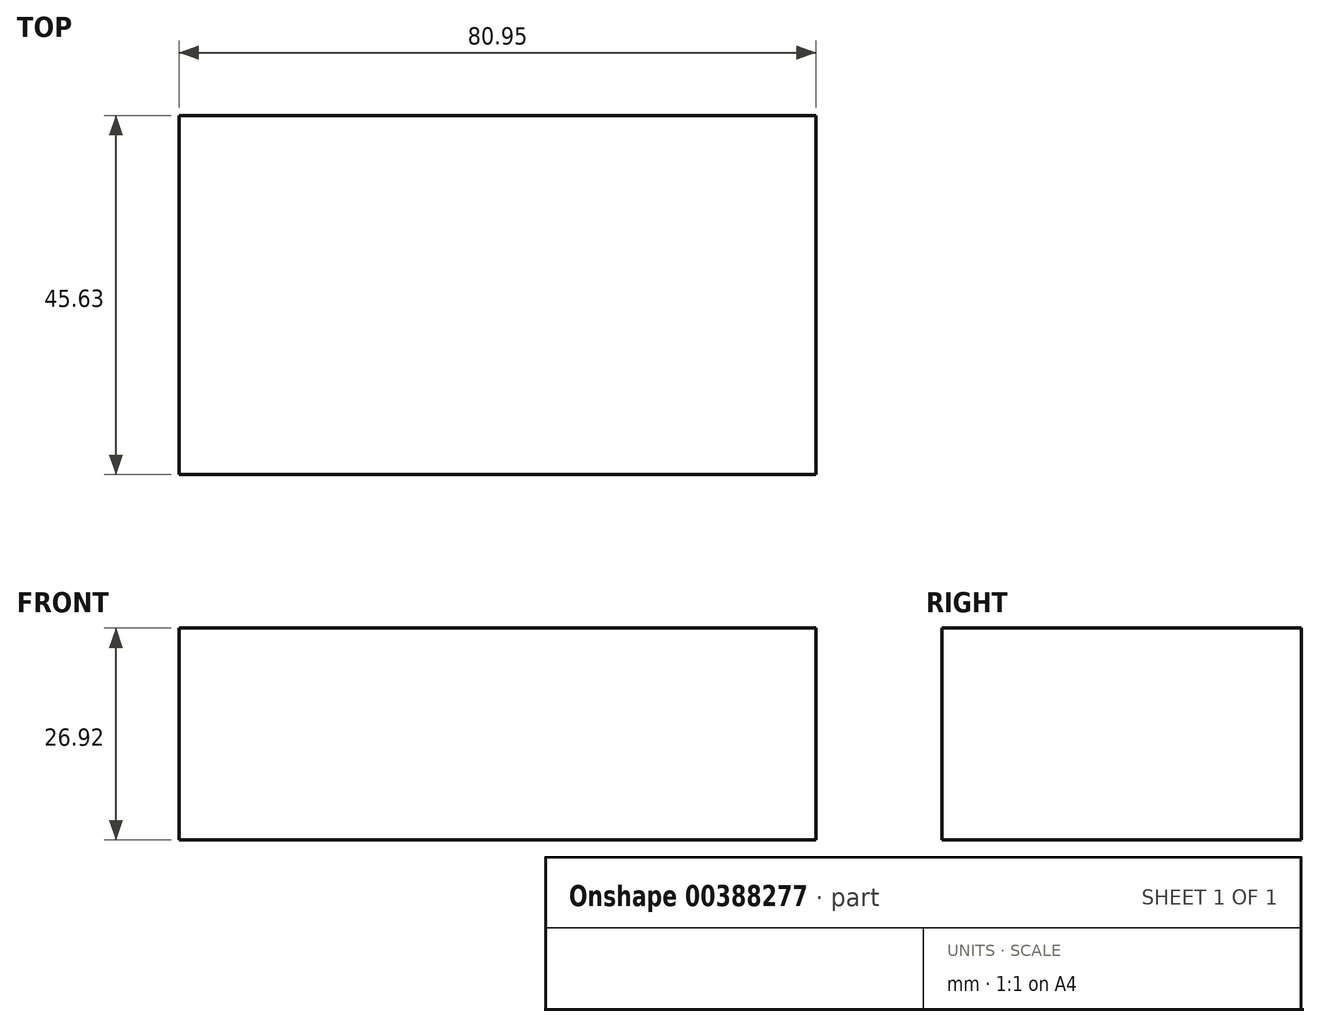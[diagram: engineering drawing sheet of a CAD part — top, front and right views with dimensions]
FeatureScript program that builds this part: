
annotation { "Feature Type Name" : "Feature", "Feature Type Description" : "" }
export const myFeature = defineFeature(function(context is Context, id is Id, definition is map)
    precondition{}
    {
        {
            var Q0;
            Q0=qCreatedBy(makeId("Top.planeOp"),FACE);
            var sketch = newSketch(context, id + "F0", { "sketchPlane" : qUnion([Q0])});
            skLineSegment(sketch, "E0.bottom", {"start": v(-36.53, 32.71) * mm, "end": v(44.42, 32.71) * mm});
            skLineSegment(sketch, "E0.top", {"start": v(-36.53, -12.92) * mm, "end": v(44.42, -12.92) * mm});
            skLineSegment(sketch, "E0.left", {"start": v(-36.53, 32.71) * mm, "end": v(-36.53, -12.92) * mm});
            skLineSegment(sketch, "E0.right", {"start": v(44.42, 32.71) * mm, "end": v(44.42, -12.92) * mm});
            skSolve(sketch);
        }
        {
            var Q0;
            Q0 = qSketchRegion(id + "F0", true);
            extrude(context, id + "F1", {"entities" : qUnion([Q0]), "depth" : 26.92 * mm});
        }
        {
            var Q0;
            Q0=qCreatedBy(makeId("Top.planeOp"),FACE);
            var sketch = newSketch(context, id + "F2", { "sketchPlane" : qUnion([Q0])});
            skLineSegment(sketch, "E1.bottom", {"start": v(-26.19, 23.43) * mm, "end": v(-20, 23.43) * mm});
            skLineSegment(sketch, "E1.top", {"start": v(-26.19, 0) * mm, "end": v(-20, 0) * mm});
            skLineSegment(sketch, "E1.left", {"start": v(-26.19, 23.43) * mm, "end": v(-26.19, 0) * mm});
            skLineSegment(sketch, "E1.right", {"start": v(-20, 23.43) * mm, "end": v(-20, 0) * mm});
            skArc(sketch, "E2", {"start": v(-20, 23.43) * mm, "mid": v(-23.1, 26.52) * mm, "end": v(-26.19, 23.43) * mm});
            skArc(sketch, "E3", {"start": v(-26.19, 0) * mm, "mid": v(-23.1, -3.1) * mm, "end": v(-20, 0) * mm});
            skSolve(sketch);
        }
        {
            var Q0;
            Q0 = qSketchRegion(id + "F2", true);
            extrude(context, id + "F3", {"entities" : qUnion([Q0]), "operationType" : NewBodyOperationType.ADD, "depth" : 25.4 * mm});
        }
        {
            var Q0;
            Q0=qCreatedBy(makeId("Top.planeOp"),FACE);
            var sketch = newSketch(context, id + "F4", { "sketchPlane" : qUnion([Q0])});
            skCircle(sketch, "E4", {"center": v(21.25, 9) * mm, "radius": 10.2 * mm});
            skSolve(sketch);
        }
        {
            var Q0;
            Q0 = qSketchRegion(id + "F4", true);
            extrude(context, id + "F5", {"entities" : qUnion([Q0]), "operationType" : NewBodyOperationType.ADD, "depth" : 26.92 * mm});
        }
    });
